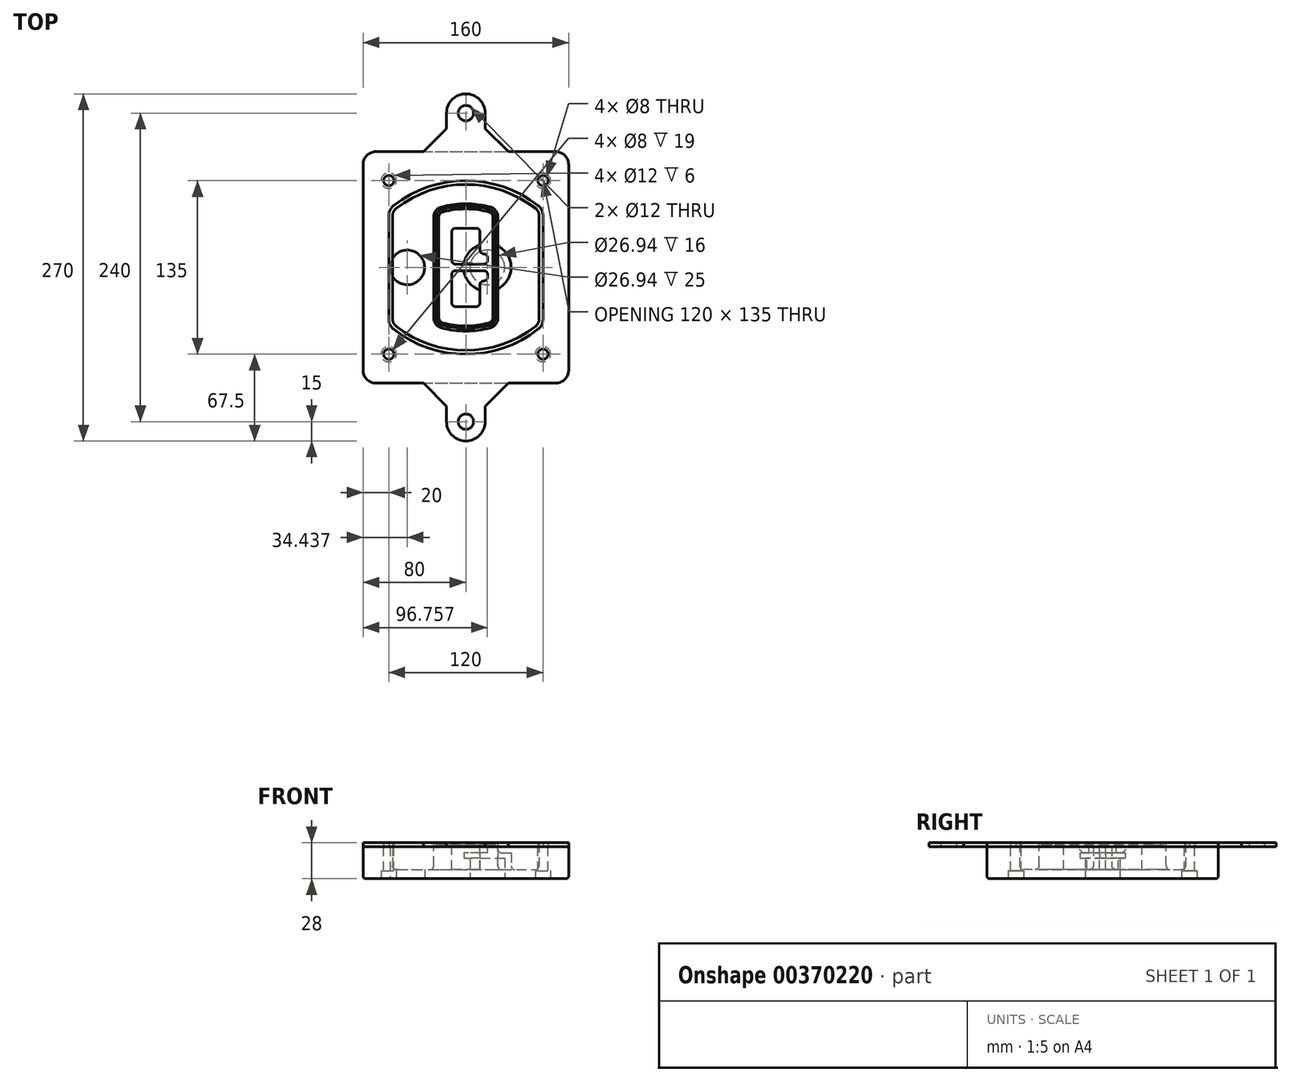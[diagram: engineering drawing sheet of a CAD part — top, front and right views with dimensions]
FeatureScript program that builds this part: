
annotation { "Feature Type Name" : "Feature", "Feature Type Description" : "" }
export const myFeature = defineFeature(function(context is Context, id is Id, definition is map)
    precondition{}
    {
        {
            var Q0;
            Q0=qCreatedBy(makeId("Top.planeOp"),FACE);
            var sketch = newSketch(context, id + "F0", { "sketchPlane" : qUnion([Q0])});
            skPoint(sketch, "E0.rect.middle", {"position": v(0, 0) * mm});
            skLineSegment(sketch, "E1.bottom", {"start": v(-70, -90) * mm, "end": v(70, -90) * mm});
            skLineSegment(sketch, "E1.top", {"start": v(-70, 90) * mm, "end": v(70, 90) * mm});
            skLineSegment(sketch, "E1.left", {"start": v(-80, -80) * mm, "end": v(-80, 80) * mm});
            skLineSegment(sketch, "E1.right", {"start": v(80, -80) * mm, "end": v(80, 80) * mm});
            skLineSegment(sketch, "E2", {"start": v(-80, 90) * mm, "end": v(80, -90) * mm, "construction": true});
            skLineSegment(sketch, "E3", {"start": v(80, 90) * mm, "end": v(-80, -90) * mm, "construction": true});
            skCircle(sketch, "E4", {"center": v(-60, 67.5) * mm, "radius": 4 * mm});
            skCircle(sketch, "E5", {"center": v(60, 67.5) * mm, "radius": 4 * mm});
            skCircle(sketch, "E6", {"center": v(60, -67.5) * mm, "radius": 4 * mm});
            skCircle(sketch, "E7", {"center": v(-60, -67.5) * mm, "radius": 4 * mm});
            skLineSegment(sketch, "E8", {"start": v(-60, 67.5) * mm, "end": v(60, 67.5) * mm, "construction": true});
            skLineSegment(sketch, "E9", {"start": v(60, 67.5) * mm, "end": v(60, -67.5) * mm, "construction": true});
            skLineSegment(sketch, "E10", {"start": v(60, -67.5) * mm, "end": v(-60, -67.5) * mm, "construction": true});
            skLineSegment(sketch, "E11", {"start": v(-60, -67.5) * mm, "end": v(-60, 67.5) * mm, "construction": true});
            skLineSegment(sketch, "E12", {"start": v(-60, 40.3) * mm, "end": v(-60, -40.3) * mm});
            skLineSegment(sketch, "E13", {"start": v(60, 40.3) * mm, "end": v(60, -40.3) * mm});
            skArc(sketch, "E14", {"start": v(56.15, 48.18) * mm, "mid": v(0, 67.5) * mm, "end": v(-56.15, 48.18) * mm});
            skArc(sketch, "E15", {"start": v(-56.15, -48.18) * mm, "mid": v(0, -67.5) * mm, "end": v(56.15, -48.18) * mm});
            skLineSegment(sketch, "E16", {"start": v(-60, 0) * mm, "end": v(60, 0) * mm, "construction": true});
            skPoint(sketch, "E17.visualSharp", {"position": v(-60, -45) * mm});
            skArc(sketch, "E17.filletArc", {"start": v(-60, -40.3) * mm, "mid": v(-58.99, -44.68) * mm, "end": v(-56.15, -48.18) * mm});
            skPoint(sketch, "E18.visualSharp", {"position": v(-60, 45) * mm});
            skArc(sketch, "E18.filletArc", {"start": v(-56.15, 48.18) * mm, "mid": v(-58.99, 44.68) * mm, "end": v(-60, 40.3) * mm});
            skPoint(sketch, "E19.visualSharp", {"position": v(60, 45) * mm});
            skArc(sketch, "E19.filletArc", {"start": v(60, 40.3) * mm, "mid": v(58.99, 44.68) * mm, "end": v(56.15, 48.18) * mm});
            skPoint(sketch, "E20.visualSharp", {"position": v(60, -45) * mm});
            skArc(sketch, "E20.filletArc", {"start": v(56.15, -48.18) * mm, "mid": v(58.99, -44.68) * mm, "end": v(60, -40.3) * mm});
            skPoint(sketch, "E21.visualSharp", {"position": v(-80, 90) * mm});
            skArc(sketch, "E21.filletArc", {"start": v(-70, 90) * mm, "mid": v(-77.07, 87.07) * mm, "end": v(-80, 80) * mm});
            skPoint(sketch, "E22.visualSharp", {"position": v(80, 90) * mm});
            skArc(sketch, "E22.filletArc", {"start": v(80, 80) * mm, "mid": v(77.07, 87.07) * mm, "end": v(70, 90) * mm});
            skPoint(sketch, "E23.visualSharp", {"position": v(80, -90) * mm});
            skArc(sketch, "E23.filletArc", {"start": v(70, -90) * mm, "mid": v(77.07, -87.07) * mm, "end": v(80, -80) * mm});
            skPoint(sketch, "E24.visualSharp", {"position": v(-80, -90) * mm});
            skArc(sketch, "E24.filletArc", {"start": v(-80, -80) * mm, "mid": v(-77.07, -87.07) * mm, "end": v(-70, -90) * mm});
            skArc(sketch, "E25.0", {"start": v(57, 40.3) * mm, "mid": v(56.3, 43.36) * mm, "end": v(54.3, 45.81) * mm});
            skLineSegment(sketch, "E25.1", {"start": v(57, 40.3) * mm, "end": v(57, -40.3) * mm});
            skArc(sketch, "E25.2", {"start": v(54.3, -45.81) * mm, "mid": v(56.3, -43.36) * mm, "end": v(57, -40.3) * mm});
            skArc(sketch, "E25.3", {"start": v(-54.3, -45.81) * mm, "mid": v(0, -64.5) * mm, "end": v(54.3, -45.81) * mm});
            skArc(sketch, "E25.4", {"start": v(-57, -40.3) * mm, "mid": v(-56.3, -43.36) * mm, "end": v(-54.3, -45.81) * mm});
            skArc(sketch, "E25.5", {"start": v(54.3, 45.81) * mm, "mid": v(0, 64.5) * mm, "end": v(-54.3, 45.81) * mm});
            skLineSegment(sketch, "E25.6", {"start": v(-57, 40.3) * mm, "end": v(-57, -40.3) * mm});
            skArc(sketch, "E25.7", {"start": v(-54.3, 45.81) * mm, "mid": v(-56.3, 43.36) * mm, "end": v(-57, 40.3) * mm});
            skArc(sketch, "E26.0", {"start": v(-58.62, 51.33) * mm, "mid": v(-62.58, 46.43) * mm, "end": v(-64, 40.3) * mm});
            skArc(sketch, "E26.1", {"start": v(58.62, 51.33) * mm, "mid": v(0, 71.5) * mm, "end": v(-58.62, 51.33) * mm});
            skArc(sketch, "E26.2", {"start": v(64, 40.3) * mm, "mid": v(62.58, 46.43) * mm, "end": v(58.62, 51.33) * mm});
            skLineSegment(sketch, "E26.3", {"start": v(64, 40.3) * mm, "end": v(64, -40.3) * mm});
            skArc(sketch, "E26.4", {"start": v(58.62, -51.33) * mm, "mid": v(62.58, -46.43) * mm, "end": v(64, -40.3) * mm});
            skLineSegment(sketch, "E26.5", {"start": v(-64, 40.3) * mm, "end": v(-64, -40.3) * mm});
            skArc(sketch, "E26.6", {"start": v(-58.62, -51.33) * mm, "mid": v(0, -71.5) * mm, "end": v(58.62, -51.33) * mm});
            skArc(sketch, "E26.7", {"start": v(-64, -40.3) * mm, "mid": v(-62.58, -46.43) * mm, "end": v(-58.62, -51.33) * mm});
            skSolve(sketch);
        }
        {
            var Q0;
            Q0=makeQuery(id+"F0.imprint","IMPRINT",FACE,{"disambiguationData":[TD([[makeQuery(id+"F0.imprint","IMPRINT",EDGE,{"derivedFrom":sQuery(id+"F0.wireOp",EDGE,"E1.bottom")}),1.0]])]});
            var Q1;
            Q1=makeQuery(id+"F0.imprint","IMPRINT",FACE,{"disambiguationData":[TD([[makeQuery(id+"F0.imprint","IMPRINT",EDGE,{"derivedFrom":sQuery(id+"F0.wireOp",EDGE,"E12")}),1.0]])]});
            var Q2;
            Q2=makeQuery(id+"F0.imprint","IMPRINT",FACE,{"disambiguationData":[TD([[makeQuery(id+"F0.imprint","IMPRINT",EDGE,{"derivedFrom":sQuery(id+"F0.wireOp",EDGE,"E25.0")}),1.0]])]});
            var Q3;
            Q3=makeQuery(id+"F0.imprint","IMPRINT",FACE,{"disambiguationData":[TD([[makeQuery(id+"F0.imprint","IMPRINT",EDGE,{"derivedFrom":sQuery(id+"F0.wireOp",EDGE,"E12")}),-1.0]])]});
            extrude(context, id + "F1", {"entities" : qUnion([Q0, Q1, Q2, Q3]), "oppositeDirection" : true, "depth" : 25 * mm});
        }
        {
            var Q0;
            Q0=makeQuery(id+"F0.imprint","IMPRINT",FACE,{"disambiguationData":[TD([[makeQuery(id+"F0.imprint","IMPRINT",EDGE,{"derivedFrom":sQuery(id+"F0.wireOp",EDGE,"E12")}),1.0]])]});
            extrude(context, id + "F2", {"entities" : qUnion([Q0]), "operationType" : NewBodyOperationType.ADD, "depth" : 3 * mm});
        }
        {
            var Q0;
            Q0=makeQuery(id+"F0.imprint","IMPRINT",FACE,{"disambiguationData":[TD([[makeQuery(id+"F0.imprint","IMPRINT",EDGE,{"derivedFrom":sQuery(id+"F0.wireOp",EDGE,"E25.0")}),1.0]])]});
            extrude(context, id + "F3", {"entities" : qUnion([Q0]), "operationType" : NewBodyOperationType.REMOVE, "oppositeDirection" : true, "depth" : 18 * mm});
        }
        {
            var Q0;
            Q0=makeQuery(id+"F2.opExtrude","CAP_FACE",FACE,{"disambiguationData":[OSD([sQuery(id+"F0.wireOp",EDGE,"E12"),sQuery(id+"F0.wireOp",EDGE,"E13"),sQuery(id+"F0.wireOp",EDGE,"E14"),sQuery(id+"F0.wireOp",EDGE,"E15"),sQuery(id+"F0.wireOp",EDGE,"E17.filletArc"),sQuery(id+"F0.wireOp",EDGE,"E18.filletArc"),sQuery(id+"F0.wireOp",EDGE,"E19.filletArc"),sQuery(id+"F0.wireOp",EDGE,"E20.filletArc"),sQuery(id+"F0.wireOp",EDGE,"E25.0"),sQuery(id+"F0.wireOp",EDGE,"E25.1"),sQuery(id+"F0.wireOp",EDGE,"E25.2"),sQuery(id+"F0.wireOp",EDGE,"E25.3"),sQuery(id+"F0.wireOp",EDGE,"E25.4"),sQuery(id+"F0.wireOp",EDGE,"E25.5"),sQuery(id+"F0.wireOp",EDGE,"E25.6"),sQuery(id+"F0.wireOp",EDGE,"E25.7")])],"isStart":false});
            var sketch = newSketch(context, id + "F4", { "sketchPlane" : qUnion([Q0])});
            skArc(sketch, "E27.0", {"start": v(-19.08, -46.97) * mm, "mid": v(0, -49.5) * mm, "end": v(19.08, -46.97) * mm});
            skArc(sketch, "E28.0", {"start": v(19.08, 46.97) * mm, "mid": v(0, 49.5) * mm, "end": v(-19.08, 46.97) * mm});
            skLineSegment(sketch, "E29", {"start": v(-25, 39.25) * mm, "end": v(-25, -39.25) * mm});
            skLineSegment(sketch, "E30", {"start": v(25, 39.25) * mm, "end": v(25, -39.25) * mm});
            skLineSegment(sketch, "E31", {"start": v(-25, 45.1) * mm, "end": v(25, 45.1) * mm, "construction": true});
            skLineSegment(sketch, "E32", {"start": v(-25, -45.1) * mm, "end": v(25, -45.1) * mm, "construction": true});
            skPoint(sketch, "E33.visualSharp", {"position": v(-25, 45.1) * mm});
            skArc(sketch, "E33.filletArc", {"start": v(-19.08, 46.97) * mm, "mid": v(-23.35, 44.11) * mm, "end": v(-25, 39.25) * mm});
            skPoint(sketch, "E34.visualSharp", {"position": v(25, 45.1) * mm});
            skArc(sketch, "E34.filletArc", {"start": v(25, 39.25) * mm, "mid": v(23.35, 44.11) * mm, "end": v(19.08, 46.97) * mm});
            skPoint(sketch, "E35.visualSharp", {"position": v(25, -45.1) * mm});
            skArc(sketch, "E35.filletArc", {"start": v(19.08, -46.97) * mm, "mid": v(23.35, -44.11) * mm, "end": v(25, -39.25) * mm});
            skPoint(sketch, "E36.visualSharp", {"position": v(-25, -45.1) * mm});
            skArc(sketch, "E36.filletArc", {"start": v(-25, -39.25) * mm, "mid": v(-23.35, -44.11) * mm, "end": v(-19.08, -46.97) * mm});
            skArc(sketch, "E37.0", {"start": v(54.3, 45.81) * mm, "mid": v(0, 64.5) * mm, "end": v(-54.3, 45.81) * mm});
            skArc(sketch, "E37.1", {"start": v(-54.3, 45.81) * mm, "mid": v(-56.3, 43.36) * mm, "end": v(-57, 40.3) * mm});
            skLineSegment(sketch, "E37.2", {"start": v(-57, 40.3) * mm, "end": v(-57, -40.3) * mm});
            skArc(sketch, "E37.3", {"start": v(-57, -40.3) * mm, "mid": v(-56.3, -43.36) * mm, "end": v(-54.3, -45.81) * mm});
            skArc(sketch, "E37.4", {"start": v(-54.3, -45.81) * mm, "mid": v(0, -64.5) * mm, "end": v(54.3, -45.81) * mm});
            skArc(sketch, "E37.5", {"start": v(54.3, -45.81) * mm, "mid": v(56.3, -43.36) * mm, "end": v(57, -40.3) * mm});
            skLineSegment(sketch, "E37.6", {"start": v(57, 40.3) * mm, "end": v(57, -40.3) * mm});
            skArc(sketch, "E37.7", {"start": v(57, 40.3) * mm, "mid": v(56.3, 43.36) * mm, "end": v(54.3, 45.81) * mm});
            skLineSegment(sketch, "E38.0", {"start": v(23, 39.25) * mm, "end": v(23, -39.25) * mm});
            skArc(sketch, "E38.1", {"start": v(18.56, -45.04) * mm, "mid": v(21.76, -42.9) * mm, "end": v(23, -39.25) * mm});
            skArc(sketch, "E38.2", {"start": v(-18.56, -45.04) * mm, "mid": v(0, -47.5) * mm, "end": v(18.56, -45.04) * mm});
            skArc(sketch, "E38.3", {"start": v(-23, -39.25) * mm, "mid": v(-21.76, -42.9) * mm, "end": v(-18.56, -45.04) * mm});
            skLineSegment(sketch, "E38.4", {"start": v(-23, 39.25) * mm, "end": v(-23, -39.25) * mm});
            skArc(sketch, "E38.5", {"start": v(23, 39.25) * mm, "mid": v(21.76, 42.9) * mm, "end": v(18.56, 45.04) * mm});
            skArc(sketch, "E38.6", {"start": v(-18.56, 45.04) * mm, "mid": v(-21.76, 42.9) * mm, "end": v(-23, 39.25) * mm});
            skArc(sketch, "E38.7", {"start": v(18.56, 45.04) * mm, "mid": v(0, 47.5) * mm, "end": v(-18.56, 45.04) * mm});
            skArc(sketch, "E39.0", {"start": v(21, 39.25) * mm, "mid": v(20.18, 41.68) * mm, "end": v(18.04, 43.1) * mm});
            skLineSegment(sketch, "E39.1", {"start": v(21, 39.25) * mm, "end": v(21, -39.25) * mm});
            skArc(sketch, "E39.2", {"start": v(18.04, -43.1) * mm, "mid": v(20.18, -41.68) * mm, "end": v(21, -39.25) * mm});
            skArc(sketch, "E39.3", {"start": v(-18.04, -43.1) * mm, "mid": v(0, -45.5) * mm, "end": v(18.04, -43.1) * mm});
            skArc(sketch, "E39.4", {"start": v(-21, -39.25) * mm, "mid": v(-20.18, -41.68) * mm, "end": v(-18.04, -43.1) * mm});
            skArc(sketch, "E39.5", {"start": v(18.04, 43.1) * mm, "mid": v(0, 45.5) * mm, "end": v(-18.04, 43.1) * mm});
            skLineSegment(sketch, "E39.6", {"start": v(-21, 39.25) * mm, "end": v(-21, -39.25) * mm});
            skArc(sketch, "E39.7", {"start": v(-18.04, 43.1) * mm, "mid": v(-20.18, 41.68) * mm, "end": v(-21, 39.25) * mm});
            skLineSegment(sketch, "E40", {"start": v(-25, 0) * mm, "end": v(25, 0) * mm, "construction": true});
            skLineSegment(sketch, "E41", {"start": v(-11, 5.5) * mm, "end": v(-11, 27.5) * mm});
            skLineSegment(sketch, "E42", {"start": v(-8, 30.5) * mm, "end": v(8, 30.5) * mm});
            skLineSegment(sketch, "E43", {"start": v(11, 27.5) * mm, "end": v(11, 13.5) * mm});
            skLineSegment(sketch, "E44", {"start": v(14, 10.5) * mm, "end": v(14, 10.5) * mm});
            skLineSegment(sketch, "E45", {"start": v(17, 7.5) * mm, "end": v(17, 5.5) * mm});
            skLineSegment(sketch, "E46", {"start": v(14, 2.5) * mm, "end": v(-8, 2.5) * mm});
            skPoint(sketch, "E47.visualSharp", {"position": v(-11, 30.5) * mm});
            skArc(sketch, "E47.filletArc", {"start": v(-8, 30.5) * mm, "mid": v(-10.12, 29.62) * mm, "end": v(-11, 27.5) * mm});
            skPoint(sketch, "E48.visualSharp", {"position": v(11, 30.5) * mm});
            skArc(sketch, "E48.filletArc", {"start": v(11, 27.5) * mm, "mid": v(10.12, 29.62) * mm, "end": v(8, 30.5) * mm});
            skPoint(sketch, "E49.visualSharp", {"position": v(11, 10.5) * mm});
            skArc(sketch, "E49.filletArc", {"start": v(11, 13.5) * mm, "mid": v(11.88, 11.38) * mm, "end": v(14, 10.5) * mm});
            skPoint(sketch, "E50.visualSharp", {"position": v(17, 10.5) * mm});
            skArc(sketch, "E50.filletArc", {"start": v(17, 7.5) * mm, "mid": v(16.12, 9.62) * mm, "end": v(14, 10.5) * mm});
            skPoint(sketch, "E51.visualSharp", {"position": v(17, 2.5) * mm});
            skArc(sketch, "E51.filletArc", {"start": v(14, 2.5) * mm, "mid": v(16.12, 3.38) * mm, "end": v(17, 5.5) * mm});
            skPoint(sketch, "E52.visualSharp", {"position": v(-11, 2.5) * mm});
            skArc(sketch, "E52.filletArc", {"start": v(-11, 5.5) * mm, "mid": v(-10.12, 3.38) * mm, "end": v(-8, 2.5) * mm});
            skLineSegment(sketch, "E53.0.MirrorCS", {"start": v(14, -2.5) * mm, "end": v(-8, -2.5) * mm});
            skArc(sketch, "E54.0.MirrorCS", {"start": v(-11, -5.5) * mm, "mid": v(-10.12, -3.38) * mm, "end": v(-8, -2.5) * mm});
            skLineSegment(sketch, "E55.0.MirrorCS", {"start": v(-11, -5.5) * mm, "end": v(-11, -27.5) * mm});
            skArc(sketch, "E56.0.MirrorCS", {"start": v(-8, -30.5) * mm, "mid": v(-10.12, -29.62) * mm, "end": v(-11, -27.5) * mm});
            skLineSegment(sketch, "E57.0.MirrorCS", {"start": v(-8, -30.5) * mm, "end": v(8, -30.5) * mm});
            skArc(sketch, "E58.0.MirrorCS", {"start": v(11, -27.5) * mm, "mid": v(10.12, -29.62) * mm, "end": v(8, -30.5) * mm});
            skLineSegment(sketch, "E59.0.MirrorCS", {"start": v(11, -27.5) * mm, "end": v(11, -13.5) * mm});
            skArc(sketch, "E60.0.MirrorCS", {"start": v(11, -13.5) * mm, "mid": v(11.88, -11.38) * mm, "end": v(14, -10.5) * mm});
            skArc(sketch, "E61.0.MirrorCS", {"start": v(17, -7.5) * mm, "mid": v(16.12, -9.62) * mm, "end": v(14, -10.5) * mm});
            skLineSegment(sketch, "E62.0.MirrorCS", {"start": v(17, -7.5) * mm, "end": v(17, -5.5) * mm});
            skArc(sketch, "E63.0.MirrorCS", {"start": v(14, -2.5) * mm, "mid": v(16.12, -3.38) * mm, "end": v(17, -5.5) * mm});
            skSolve(sketch);
        }
        {
            var Q0;
            Q0=makeQuery(id+"F4.imprint","IMPRINT",FACE,{"disambiguationData":[TD([[makeQuery(id+"F4.imprint","IMPRINT",EDGE,{"derivedFrom":sQuery(id+"F4.wireOp",EDGE,"E27.0")}),1.0]])]});
            var Q1;
            Q1=makeQuery(id+"F4.imprint","IMPRINT",FACE,{"disambiguationData":[TD([[makeQuery(id+"F4.imprint","IMPRINT",EDGE,{"derivedFrom":sQuery(id+"F4.wireOp",EDGE,"E38.0")}),-1.0]])]});
            var Q2;
            Q2=makeQuery(id+"F4.imprint","IMPRINT",FACE,{"disambiguationData":[TD([[makeQuery(id+"F4.imprint","IMPRINT",EDGE,{"derivedFrom":sQuery(id+"F4.wireOp",EDGE,"E39.0")}),1.0]])]});
            extrude(context, id + "F5", {"entities" : qUnion([Q0, Q1, Q2]), "operationType" : NewBodyOperationType.ADD, "endBound" : BoundingType.UP_TO_NEXT, "oppositeDirection" : true, "depth" : 25 * mm});
        }
        {
            var Q0;
            Q0=makeQuery(id+"F4.imprint","IMPRINT",FACE,{"disambiguationData":[TD([[makeQuery(id+"F4.imprint","IMPRINT",EDGE,{"derivedFrom":sQuery(id+"F4.wireOp",EDGE,"E38.0")}),-1.0]])]});
            extrude(context, id + "F6", {"entities" : qUnion([Q0]), "operationType" : NewBodyOperationType.REMOVE, "oppositeDirection" : true, "depth" : 2 * mm});
        }
        {
            var Q0;
            Q0=makeQuery(id+"F1.opExtrude","CAP_FACE",FACE,{"disambiguationData":[OSD([sQuery(id+"F0.wireOp",EDGE,"E1.bottom"),sQuery(id+"F0.wireOp",EDGE,"E1.top"),sQuery(id+"F0.wireOp",EDGE,"E1.left"),sQuery(id+"F0.wireOp",EDGE,"E1.right"),sQuery(id+"F0.wireOp",EDGE,"E4"),sQuery(id+"F0.wireOp",EDGE,"E5"),sQuery(id+"F0.wireOp",EDGE,"E6"),sQuery(id+"F0.wireOp",EDGE,"E7"),sQuery(id+"F0.wireOp",EDGE,"E21.filletArc"),sQuery(id+"F0.wireOp",EDGE,"E22.filletArc"),sQuery(id+"F0.wireOp",EDGE,"E23.filletArc"),sQuery(id+"F0.wireOp",EDGE,"E24.filletArc")])],"isStart":false});
            var sketch = newSketch(context, id + "F7", { "sketchPlane" : qUnion([Q0])});
            skCircle(sketch, "E64", {"center": v(16.76, 0) * mm, "radius": 13.47 * mm});
            skCircle(sketch, "E65", {"center": v(-45.56, 0) * mm, "radius": 13.47 * mm});
            skLineSegment(sketch, "E66", {"start": v(80, 0) * mm, "end": v(-80, 0) * mm});
            skCircle(sketch, "E67", {"center": v(16.76, 0) * mm, "radius": 18.47 * mm});
            skCircle(sketch, "E68", {"center": v(60, -67.5) * mm, "radius": 6 * mm});
            skCircle(sketch, "E69", {"center": v(-60, -67.5) * mm, "radius": 6 * mm});
            skCircle(sketch, "E70", {"center": v(-60, 67.5) * mm, "radius": 6 * mm});
            skCircle(sketch, "E71", {"center": v(60, 67.5) * mm, "radius": 6 * mm});
            skSolve(sketch);
        }
        {
            var Q0;
            {var subQ1=sQuery(id+"F7.wireOp",EDGE,"E66");var subQ4=sQuery(id+"F7.wireOp",EDGE,"E64");var subQ6=makeQuery(id+"F7.imprint","INTERSECT",VERTEX,{"disambiguationData":[OD(0.0)],"derivedFrom":[subQ4,subQ1]});Q0=makeQuery(id+"F7.imprint","IMPRINT",FACE,{"disambiguationData":[TD([[makeQuery(id+"F7.imprint","IMPRINT",EDGE,{"disambiguationData":[TD([[subQ6,-1.0]])],"derivedFrom":subQ4}),-1.0]])]});}
            var Q1;
            {var subQ0=sQuery(id+"F7.wireOp",EDGE,"E66");var subQ1=sQuery(id+"F7.wireOp",EDGE,"E64");var subQ3=makeQuery(id+"F7.imprint","INTERSECT",VERTEX,{"disambiguationData":[OD(0.0)],"derivedFrom":[subQ1,subQ0]});Q1=makeQuery(id+"F7.imprint","IMPRINT",FACE,{"disambiguationData":[TD([[makeQuery(id+"F7.imprint","IMPRINT",EDGE,{"disambiguationData":[TD([[subQ3,-1.0]])],"derivedFrom":subQ1}),1.0]])]});}
            var Q2;
            {var subQ0=sQuery(id+"F7.wireOp",EDGE,"E66");var subQ1=sQuery(id+"F7.wireOp",EDGE,"E64");var subQ3=makeQuery(id+"F7.imprint","INTERSECT",VERTEX,{"disambiguationData":[OD(0.0)],"derivedFrom":[subQ1,subQ0]});Q2=makeQuery(id+"F7.imprint","IMPRINT",FACE,{"disambiguationData":[TD([[makeQuery(id+"F7.imprint","IMPRINT",EDGE,{"disambiguationData":[TD([[subQ3,1.0]])],"derivedFrom":subQ1}),1.0]])]});}
            var Q3;
            {var subQ1=sQuery(id+"F7.wireOp",EDGE,"E66");var subQ4=sQuery(id+"F7.wireOp",EDGE,"E64");var subQ6=makeQuery(id+"F7.imprint","INTERSECT",VERTEX,{"disambiguationData":[OD(0.0)],"derivedFrom":[subQ4,subQ1]});Q3=makeQuery(id+"F7.imprint","IMPRINT",FACE,{"disambiguationData":[TD([[makeQuery(id+"F7.imprint","IMPRINT",EDGE,{"disambiguationData":[TD([[subQ6,1.0]])],"derivedFrom":subQ4}),-1.0]])]});}
            extrude(context, id + "F8", {"entities" : qUnion([Q0, Q1, Q2, Q3]), "operationType" : NewBodyOperationType.ADD, "oppositeDirection" : true, "depth" : 20 * mm});
        }
        {
            var Q0;
            {var subQ0=sQuery(id+"F7.wireOp",EDGE,"E66");var subQ1=sQuery(id+"F7.wireOp",EDGE,"E64");var subQ3=makeQuery(id+"F7.imprint","INTERSECT",VERTEX,{"disambiguationData":[OD(0.0)],"derivedFrom":[subQ1,subQ0]});Q0=makeQuery(id+"F7.imprint","IMPRINT",FACE,{"disambiguationData":[TD([[makeQuery(id+"F7.imprint","IMPRINT",EDGE,{"disambiguationData":[TD([[subQ3,-1.0]])],"derivedFrom":subQ1}),1.0]])]});}
            var Q1;
            {var subQ0=sQuery(id+"F7.wireOp",EDGE,"E66");var subQ1=sQuery(id+"F7.wireOp",EDGE,"E64");var subQ3=makeQuery(id+"F7.imprint","INTERSECT",VERTEX,{"disambiguationData":[OD(0.0)],"derivedFrom":[subQ1,subQ0]});Q1=makeQuery(id+"F7.imprint","IMPRINT",FACE,{"disambiguationData":[TD([[makeQuery(id+"F7.imprint","IMPRINT",EDGE,{"disambiguationData":[TD([[subQ3,1.0]])],"derivedFrom":subQ1}),1.0]])]});}
            extrude(context, id + "F9", {"entities" : qUnion([Q0, Q1]), "operationType" : NewBodyOperationType.REMOVE, "oppositeDirection" : true, "depth" : 16 * mm});
        }
        {
            var Q0;
            {var subQ0=sQuery(id+"F7.wireOp",EDGE,"E66");var subQ1=sQuery(id+"F7.wireOp",EDGE,"E65");var subQ3=makeQuery(id+"F7.imprint","INTERSECT",VERTEX,{"disambiguationData":[OD(0.0)],"derivedFrom":[subQ1,subQ0]});Q0=makeQuery(id+"F7.imprint","IMPRINT",FACE,{"disambiguationData":[TD([[makeQuery(id+"F7.imprint","IMPRINT",EDGE,{"disambiguationData":[TD([[subQ3,-1.0]])],"derivedFrom":subQ1}),1.0]])]});}
            var Q1;
            {var subQ0=sQuery(id+"F7.wireOp",EDGE,"E66");var subQ1=sQuery(id+"F7.wireOp",EDGE,"E65");var subQ3=makeQuery(id+"F7.imprint","INTERSECT",VERTEX,{"disambiguationData":[OD(0.0)],"derivedFrom":[subQ1,subQ0]});Q1=makeQuery(id+"F7.imprint","IMPRINT",FACE,{"disambiguationData":[TD([[makeQuery(id+"F7.imprint","IMPRINT",EDGE,{"disambiguationData":[TD([[subQ3,1.0]])],"derivedFrom":subQ1}),1.0]])]});}
            extrude(context, id + "F10", {"entities" : qUnion([Q0, Q1]), "operationType" : NewBodyOperationType.REMOVE, "oppositeDirection" : true, "depth" : 25 * mm});
        }
        {
            var Q0;
            Q0=makeQuery(id+"F7.imprint","IMPRINT",FACE,{"disambiguationData":[TD([[makeQuery(id+"F7.imprint","IMPRINT",EDGE,{"derivedFrom":sQuery(id+"F7.wireOp",EDGE,"E68")}),1.0]])]});
            var Q1;
            Q1=makeQuery(id+"F7.imprint","IMPRINT",FACE,{"disambiguationData":[TD([[makeQuery(id+"F7.imprint","IMPRINT",EDGE,{"derivedFrom":makeQuery(id+"F1.opExtrude","CAP_EDGE",EDGE,{"disambiguationData":[OSD([sQuery(id+"F0.wireOp",EDGE,"E5")])],"isStart":false})}),-1.0]])]});
            var Q2;
            Q2=makeQuery(id+"F7.imprint","IMPRINT",FACE,{"disambiguationData":[TD([[makeQuery(id+"F7.imprint","IMPRINT",EDGE,{"derivedFrom":sQuery(id+"F7.wireOp",EDGE,"E69")}),1.0]])]});
            var Q3;
            Q3=makeQuery(id+"F7.imprint","IMPRINT",FACE,{"disambiguationData":[TD([[makeQuery(id+"F7.imprint","IMPRINT",EDGE,{"derivedFrom":makeQuery(id+"F1.opExtrude","CAP_EDGE",EDGE,{"disambiguationData":[OSD([sQuery(id+"F0.wireOp",EDGE,"E4")])],"isStart":false})}),-1.0]])]});
            var Q4;
            Q4=makeQuery(id+"F7.imprint","IMPRINT",FACE,{"disambiguationData":[TD([[makeQuery(id+"F7.imprint","IMPRINT",EDGE,{"derivedFrom":sQuery(id+"F7.wireOp",EDGE,"E70")}),1.0]])]});
            var Q5;
            Q5=makeQuery(id+"F7.imprint","IMPRINT",FACE,{"disambiguationData":[TD([[makeQuery(id+"F7.imprint","IMPRINT",EDGE,{"derivedFrom":makeQuery(id+"F1.opExtrude","CAP_EDGE",EDGE,{"disambiguationData":[OSD([sQuery(id+"F0.wireOp",EDGE,"E7")])],"isStart":false})}),-1.0]])]});
            var Q6;
            Q6=makeQuery(id+"F7.imprint","IMPRINT",FACE,{"disambiguationData":[TD([[makeQuery(id+"F7.imprint","IMPRINT",EDGE,{"derivedFrom":sQuery(id+"F7.wireOp",EDGE,"E71")}),1.0]])]});
            var Q7;
            Q7=makeQuery(id+"F7.imprint","IMPRINT",FACE,{"disambiguationData":[TD([[makeQuery(id+"F7.imprint","IMPRINT",EDGE,{"derivedFrom":makeQuery(id+"F1.opExtrude","CAP_EDGE",EDGE,{"disambiguationData":[OSD([sQuery(id+"F0.wireOp",EDGE,"E6")])],"isStart":false})}),-1.0]])]});
            extrude(context, id + "F11", {"entities" : qUnion([Q0, Q1, Q2, Q3, Q4, Q5, Q6, Q7]), "operationType" : NewBodyOperationType.REMOVE, "oppositeDirection" : true, "depth" : 6 * mm});
        }
        {
            var Q0;
            Q0=makeQuery(id+"F9.boolean.opBoolean","COPY",FACE,{"derivedFrom":makeQuery(id+"F9.opExtrude","CAP_FACE",FACE,{"disambiguationData":[OSD([sQuery(id+"F7.wireOp",EDGE,"E64")])],"isStart":false})});
            var sketch = newSketch(context, id + "F12", { "sketchPlane" : qUnion([Q0])});
            skArc(sketch, "E72.0", {"start": v(11, 17.55) * mm, "mid": v(2.57, 11.82) * mm, "end": v(-1.54, 2.5) * mm});
            skArc(sketch, "E72.1", {"start": v(-1.54, -2.5) * mm, "mid": v(2.57, -11.82) * mm, "end": v(11, -17.55) * mm});
            skLineSegment(sketch, "E73", {"start": v(-1.54, -2.5) * mm, "end": v(14, -2.5) * mm});
            skLineSegment(sketch, "E74.0", {"start": v(14, 2.5) * mm, "end": v(-1.54, 2.5) * mm});
            skArc(sketch, "E74.1", {"start": v(14, 2.5) * mm, "mid": v(16.12, 3.38) * mm, "end": v(17, 5.5) * mm});
            skLineSegment(sketch, "E74.2", {"start": v(17, 7.5) * mm, "end": v(17, 5.5) * mm});
            skArc(sketch, "E74.3", {"start": v(17, 7.5) * mm, "mid": v(16.12, 9.62) * mm, "end": v(14, 10.5) * mm});
            skArc(sketch, "E74.4", {"start": v(11, 13.5) * mm, "mid": v(11.88, 11.38) * mm, "end": v(14, 10.5) * mm});
            skLineSegment(sketch, "E74.5", {"start": v(11, 17.55) * mm, "end": v(11, 13.5) * mm});
            skLineSegment(sketch, "E74.7", {"start": v(14, -2.5) * mm, "end": v(-1.54, -2.5) * mm});
            skArc(sketch, "E74.8", {"start": v(14, -2.5) * mm, "mid": v(16.12, -3.38) * mm, "end": v(17, -5.5) * mm});
            skLineSegment(sketch, "E74.9", {"start": v(17, -7.5) * mm, "end": v(17, -5.5) * mm});
            skArc(sketch, "E74.10", {"start": v(17, -7.5) * mm, "mid": v(16.12, -9.62) * mm, "end": v(14, -10.5) * mm});
            skArc(sketch, "E74.11", {"start": v(11, -13.5) * mm, "mid": v(11.88, -11.38) * mm, "end": v(14, -10.5) * mm});
            skLineSegment(sketch, "E74.12", {"start": v(11, -17.55) * mm, "end": v(11, -13.5) * mm});
            skPoint(sketch, "E75.orphan", {"position": v(11, -27.5) * mm});
            skPoint(sketch, "E76.orphan", {"position": v(-8, -2.5) * mm});
            skPoint(sketch, "E77.orphan", {"position": v(-8, 2.5) * mm});
            skPoint(sketch, "E78.orphan", {"position": v(11, 27.5) * mm});
            skSolve(sketch);
        }
        {
            var Q0;
            {var subQ7=sQuery(id+"F12.wireOp",EDGE,"E72.0");var subQ14=sQuery(id+"F12.wireOp",EDGE,"E72.1");var subQ16=sQuery(id+"F12.wireOp",EDGE,"E74.1");var subQ18=sQuery(id+"F12.wireOp",EDGE,"E74.8");Q0=qUnion([makeQuery(id+"F12.imprint","IMPRINT",FACE,{"disambiguationData":[TD([[makeQuery(id+"F12.imprint","IMPRINT",EDGE,{"derivedFrom":subQ7}),1.0]])]}),makeQuery(id+"F12.imprint","IMPRINT",FACE,{"disambiguationData":[TD([[makeQuery(id+"F12.imprint","IMPRINT",EDGE,{"derivedFrom":subQ14}),1.0]])]}),makeQuery(id+"F12.imprint","IMPRINT",FACE,{"disambiguationData":[TD([[makeQuery(id+"F12.imprint","IMPRINT",EDGE,{"derivedFrom":subQ16}),1.0]])]}),makeQuery(id+"F12.imprint","IMPRINT",FACE,{"disambiguationData":[TD([[makeQuery(id+"F12.imprint","IMPRINT",EDGE,{"derivedFrom":subQ18}),-1.0]])]})]);}
            var Q1;
            Q1=makeQuery(id+"F5.boolean.opBoolean","SPLIT",FACE,{"disambiguationData":[TD([makeQuery(id+"F5.opExtrude","SWEPT_FACE",FACE,{"disambiguationData":[OSD([sQuery(id+"F4.wireOp",EDGE,"E41")])]})])],"derivedFrom":makeQuery(id+"F3.boolean.opBoolean","COPY",FACE,{"derivedFrom":makeQuery(id+"F3.opExtrude","CAP_FACE",FACE,{"disambiguationData":[OSD([sQuery(id+"F0.wireOp",EDGE,"E25.0"),sQuery(id+"F0.wireOp",EDGE,"E25.1"),sQuery(id+"F0.wireOp",EDGE,"E25.2"),sQuery(id+"F0.wireOp",EDGE,"E25.3"),sQuery(id+"F0.wireOp",EDGE,"E25.4"),sQuery(id+"F0.wireOp",EDGE,"E25.5"),sQuery(id+"F0.wireOp",EDGE,"E25.6"),sQuery(id+"F0.wireOp",EDGE,"E25.7")])],"isStart":false})})});
            extrude(context, id + "F13", {"entities" : qUnion([Q0]), "operationType" : NewBodyOperationType.REMOVE, "endBound" : BoundingType.UP_TO_SURFACE, "endBoundEntityFace" : qUnion([Q1]), "depth" : 25 * mm});
        }
        {
            var Q0;
            Q0=makeQuery(id+"F3.boolean.opBoolean","COPY",EDGE,{"derivedFrom":makeQuery(id+"F3.opExtrude","CAP_EDGE",EDGE,{"disambiguationData":[OSD([sQuery(id+"F0.wireOp",EDGE,"E25.6")])],"isStart":false})});
            var Q1;
            Q1=makeQuery(id+"F8.boolean.opBoolean","INTERSECT",EDGE,{"derivedFrom":[makeQuery(id+"F5.opExtrude","SWEPT_FACE",FACE,{"disambiguationData":[OSD([sQuery(id+"F4.wireOp",EDGE,"E30")])]}),makeQuery(id+"F8.opExtrude","CAP_FACE",FACE,{"disambiguationData":[OSD([sQuery(id+"F7.wireOp",EDGE,"E67")])],"isStart":false})]});
            var Q2;
            Q2=makeQuery(id+"F8.boolean.opBoolean","INTERSECT",EDGE,{"disambiguationData":[OD(1.0)],"derivedFrom":[makeQuery(id+"F5.opExtrude","SWEPT_FACE",FACE,{"disambiguationData":[OSD([sQuery(id+"F4.wireOp",EDGE,"E30")])]}),makeQuery(id+"F8.opExtrude","SWEPT_FACE",FACE,{"disambiguationData":[OSD([sQuery(id+"F7.wireOp",EDGE,"E67")])]})]});
            var Q3;
            {var subQ0=sQuery(id+"F4.wireOp",EDGE,"E30");Q3=makeQuery(id+"F8.boolean.opBoolean","SPLIT",EDGE,{"disambiguationData":[TD([makeQuery(id+"F5.opExtrude","SWEPT_FACE",FACE,{"disambiguationData":[OSD([sQuery(id+"F4.wireOp",EDGE,"E35.filletArc")])]})])],"derivedFrom":makeQuery(id+"F5.opExtrude","CAP_EDGE",EDGE,{"disambiguationData":[OSD([subQ0])],"isStart":false})});}
            var Q4;
            {var subQ0=sQuery(id+"F0.wireOp",EDGE,"E25.7");var subQ1=sQuery(id+"F0.wireOp",EDGE,"E25.1");var subQ2=sQuery(id+"F0.wireOp",EDGE,"E25.6");var subQ3=sQuery(id+"F0.wireOp",EDGE,"E25.5");var subQ4=sQuery(id+"F0.wireOp",EDGE,"E25.4");var subQ5=sQuery(id+"F0.wireOp",EDGE,"E25.0");var subQ6=sQuery(id+"F0.wireOp",EDGE,"E25.2");var subQ7=sQuery(id+"F0.wireOp",EDGE,"E25.3");Q4=makeQuery(id+"F8.boolean.opBoolean","INTERSECT",EDGE,{"derivedFrom":[makeQuery(id+"F5.boolean.opBoolean","SPLIT",FACE,{"disambiguationData":[TD([makeQuery(id+"F2.opExtrude","SWEPT_FACE",FACE,{"disambiguationData":[OSD([subQ5])]})])],"derivedFrom":makeQuery(id+"F3.boolean.opBoolean","COPY",FACE,{"derivedFrom":makeQuery(id+"F3.opExtrude","CAP_FACE",FACE,{"disambiguationData":[OSD([subQ5,subQ1,subQ6,subQ7,subQ4,subQ3,subQ2,subQ0])],"isStart":false})})}),makeQuery(id+"F8.opExtrude","SWEPT_FACE",FACE,{"disambiguationData":[OSD([sQuery(id+"F7.wireOp",EDGE,"E67")])]})]});}
            var Q5;
            Q5=makeQuery(id+"F8.boolean.opBoolean","INTERSECT",EDGE,{"disambiguationData":[OD(0.0)],"derivedFrom":[makeQuery(id+"F5.opExtrude","SWEPT_FACE",FACE,{"disambiguationData":[OSD([sQuery(id+"F4.wireOp",EDGE,"E30")])]}),makeQuery(id+"F8.opExtrude","SWEPT_FACE",FACE,{"disambiguationData":[OSD([sQuery(id+"F7.wireOp",EDGE,"E67")])]})]});
            fillet(context, id + "F14", {"entities" : qUnion([Q0, Q1, Q2, Q3, Q4, Q5]), "radius" : 3 * mm, "tangentPropagation" : true, "allowEdgeOverflow" : false});
        }
        {
            var Q0;
            Q0=makeQuery(id+"F1.opExtrude","CAP_EDGE",EDGE,{"disambiguationData":[OSD([sQuery(id+"F0.wireOp",EDGE,"E1.bottom")])],"isStart":false});
            fillet(context, id + "F15", {"entities" : qUnion([Q0]), "radius" : 2 * mm, "tangentPropagation" : true, "allowEdgeOverflow" : false});
        }
        {
            var Q0;
            {var subQ0=sQuery(id+"F0.wireOp",EDGE,"E21.filletArc");var subQ1=sQuery(id+"F0.wireOp",EDGE,"E7");var subQ2=sQuery(id+"F0.wireOp",EDGE,"E6");var subQ3=sQuery(id+"F0.wireOp",EDGE,"E5");var subQ4=sQuery(id+"F0.wireOp",EDGE,"E4");var subQ5=sQuery(id+"F0.wireOp",EDGE,"E22.filletArc");var subQ6=sQuery(id+"F0.wireOp",EDGE,"E1.bottom");var subQ7=sQuery(id+"F0.wireOp",EDGE,"E1.right");var subQ8=sQuery(id+"F0.wireOp",EDGE,"E1.top");var subQ9=sQuery(id+"F0.wireOp",EDGE,"E1.left");var subQ10=sQuery(id+"F0.wireOp",EDGE,"E23.filletArc");var subQ11=sQuery(id+"F0.wireOp",EDGE,"E24.filletArc");Q0=makeQuery(id+"F2.boolean.opBoolean","SPLIT",FACE,{"disambiguationData":[TD([makeQuery(id+"F1.opExtrude","SWEPT_FACE",FACE,{"disambiguationData":[OSD([subQ6])]})])],"derivedFrom":makeQuery(id+"F1.opExtrude","CAP_FACE",FACE,{"disambiguationData":[OSD([subQ6,subQ8,subQ9,subQ7,subQ4,subQ3,subQ2,subQ1,subQ0,subQ5,subQ10,subQ11])],"isStart":true})});}
            var sketch = newSketch(context, id + "F16", { "sketchPlane" : qUnion([Q0])});
            skLineSegment(sketch, "E79", {"start": v(0, 0) * mm, "end": v(0, 125.04) * mm, "construction": true});
            skCircle(sketch, "E80", {"center": v(0, 120) * mm, "radius": 6 * mm});
            skLineSegment(sketch, "E81", {"start": v(0, 120) * mm, "end": v(-80.82, 120) * mm, "construction": true});
            skLineSegment(sketch, "E82", {"start": v(0, 120) * mm, "end": v(78.12, 120) * mm, "construction": true});
            skLineSegment(sketch, "E83", {"start": v(-15, 90) * mm, "end": v(-15, 120) * mm, "construction": true});
            skLineSegment(sketch, "E84", {"start": v(15, 120) * mm, "end": v(15, 90) * mm, "construction": true});
            skArc(sketch, "E85", {"start": v(15, 120) * mm, "mid": v(0, 135) * mm, "end": v(-15, 120) * mm});
            skLineSegment(sketch, "E86", {"start": v(-15, 120) * mm, "end": v(-15, 108) * mm});
            skLineSegment(sketch, "E87", {"start": v(15, 120) * mm, "end": v(15, 108) * mm});
            skLineSegment(sketch, "E88", {"start": v(-15, 108) * mm, "end": v(-33, 90) * mm});
            skLineSegment(sketch, "E89", {"start": v(15, 108) * mm, "end": v(33, 90) * mm});
            skLineSegment(sketch, "E90", {"start": v(-80, 0) * mm, "end": v(80, 0) * mm, "construction": true});
            skLineSegment(sketch, "E91.MirrorCS", {"start": v(-15, -120) * mm, "end": v(-15, -108) * mm});
            skLineSegment(sketch, "E92.MirrorCS", {"start": v(15, -120) * mm, "end": v(15, -108) * mm});
            skLineSegment(sketch, "E93.MirrorCS", {"start": v(15, -120) * mm, "end": v(15, -90) * mm, "construction": true});
            skLineSegment(sketch, "E94.MirrorCS", {"start": v(-15, -90) * mm, "end": v(-15, -120) * mm, "construction": true});
            skArc(sketch, "E95.MirrorCS", {"start": v(15, -120) * mm, "mid": v(0, -135) * mm, "end": v(-15, -120) * mm});
            skCircle(sketch, "E96.MirrorC", {"center": v(0, -120) * mm, "radius": 6 * mm});
            skLineSegment(sketch, "E97.MirrorCS", {"start": v(-15, -108) * mm, "end": v(-33, -90) * mm});
            skLineSegment(sketch, "E98.MirrorCS", {"start": v(15, -108) * mm, "end": v(33, -90) * mm});
            skSolve(sketch);
        }
        {
            var Q0;
            Q0=makeQuery(id+"F16.imprint","IMPRINT",FACE,{"disambiguationData":[TD([[makeQuery(id+"F16.imprint","IMPRINT",EDGE,{"derivedFrom":sQuery(id+"F16.wireOp",EDGE,"E91.MirrorCS")}),-1.0]])]});
            var Q1;
            Q1=makeQuery(id+"F16.imprint","IMPRINT",FACE,{"disambiguationData":[TD([[makeQuery(id+"F16.imprint","IMPRINT",EDGE,{"derivedFrom":sQuery(id+"F16.wireOp",EDGE,"E80")}),-1.0]])]});
            var Q2;
            Q2=makeQuery(id+"F16.imprint","IMPRINT",FACE,{"disambiguationData":[TD([[makeQuery(id+"F16.imprint","IMPRINT",EDGE,{"derivedFrom":makeQuery(id+"F1.opExtrude","CAP_EDGE",EDGE,{"disambiguationData":[OSD([sQuery(id+"F0.wireOp",EDGE,"E1.left")])],"isStart":true})}),-1.0]])]});
            var Q3;
            Q3=makeQuery(id+"F2.opExtrude","CAP_FACE",FACE,{"disambiguationData":[OSD([sQuery(id+"F0.wireOp",EDGE,"E12"),sQuery(id+"F0.wireOp",EDGE,"E13"),sQuery(id+"F0.wireOp",EDGE,"E14"),sQuery(id+"F0.wireOp",EDGE,"E15"),sQuery(id+"F0.wireOp",EDGE,"E17.filletArc"),sQuery(id+"F0.wireOp",EDGE,"E18.filletArc"),sQuery(id+"F0.wireOp",EDGE,"E19.filletArc"),sQuery(id+"F0.wireOp",EDGE,"E20.filletArc"),sQuery(id+"F0.wireOp",EDGE,"E25.0"),sQuery(id+"F0.wireOp",EDGE,"E25.1"),sQuery(id+"F0.wireOp",EDGE,"E25.2"),sQuery(id+"F0.wireOp",EDGE,"E25.3"),sQuery(id+"F0.wireOp",EDGE,"E25.4"),sQuery(id+"F0.wireOp",EDGE,"E25.5"),sQuery(id+"F0.wireOp",EDGE,"E25.6"),sQuery(id+"F0.wireOp",EDGE,"E25.7")])],"isStart":false});
            extrude(context, id + "F17", {"entities" : qUnion([Q0, Q1, Q2]), "endBound" : BoundingType.UP_TO_SURFACE, "endBoundEntityFace" : qUnion([Q3]), "depth" : 25 * mm});
        }
    });
